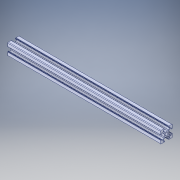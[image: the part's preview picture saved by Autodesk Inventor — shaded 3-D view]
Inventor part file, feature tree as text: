
AUTODESK INVENTOR PART (.ipt)
format: ipt  version: 2018 (Build 220112000, 112)  size: 355,328 bytes
history: native  units: in
note: dims shown in document units (in); Inventor stores cm internally (conversion verified against a paired STEP export)
features: extrude x1, sketch x1, projected_geometry x1, fillet x1
ambient origin geometry x8: Origin, YZ Plane, XZ Plane, XY Plane, X Axis, Y Axis, Z Axis, Center Point
bodies: Solid1 (feature_tree)
feature tree (4):
  extrude  "Extrusion2"  [1 undecoded]
  sketch  "Sketch3"  dims[d2=6.2992in d3=0.0in]
  projected_geometry  "Projected Loop2"
  fillet  "Fillet5"  [1 undecoded]
note: 2 required parameter values undecoded (feature->parameter linkage not recoverable at this tier; creation-order binding heuristic only, values carry confidence <= 0.55)
